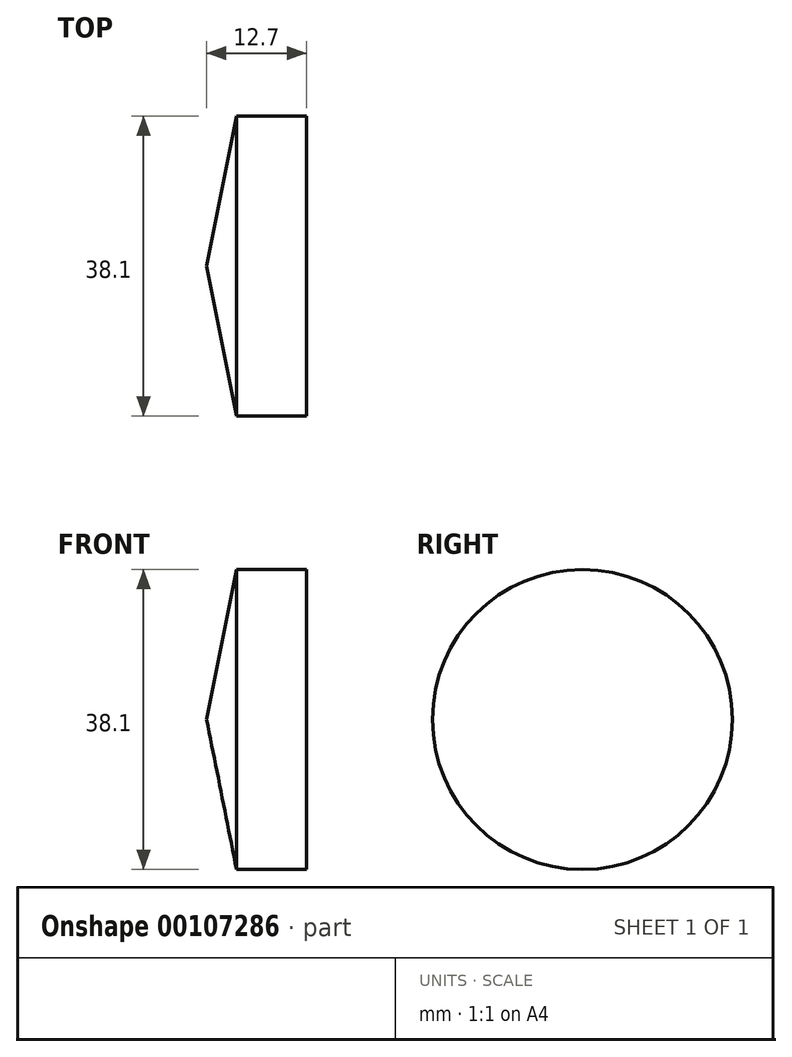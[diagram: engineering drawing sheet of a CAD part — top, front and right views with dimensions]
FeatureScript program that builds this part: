
annotation { "Feature Type Name" : "Feature", "Feature Type Description" : "" }
export const myFeature = defineFeature(function(context is Context, id is Id, definition is map)
    precondition{}
    {
        {
            var Q0;
            Q0=qCreatedBy(makeId("Front.planeOp"),FACE);
            var sketch = newSketch(context, id + "F0", { "sketchPlane" : qUnion([Q0])});
            skLineSegment(sketch, "E0", {"start": v(0, 0) * mm, "end": v(0, 19.05) * mm});
            skLineSegment(sketch, "E1", {"start": v(0, 0) * mm, "end": v(-12.7, 0) * mm});
            skLineSegment(sketch, "E2", {"start": v(-12.7, 0) * mm, "end": v(-8.9, 19.05) * mm});
            skLineSegment(sketch, "E3", {"start": v(-8.9, 19.05) * mm, "end": v(0, 19.05) * mm});
            skSolve(sketch);
        }
        {
            var Q0;
            Q0=qSketchRegion(id+"F0",true);
            var Q1;
            Q1=sQuery(id+"F0.wireOp",EDGE,"E1");
            revolve(context, id + "F1", {"entities" : qUnion([Q0]), "axis" : qUnion([Q1]), "revolveType" : RevolveType.FULL});
        }
    });
